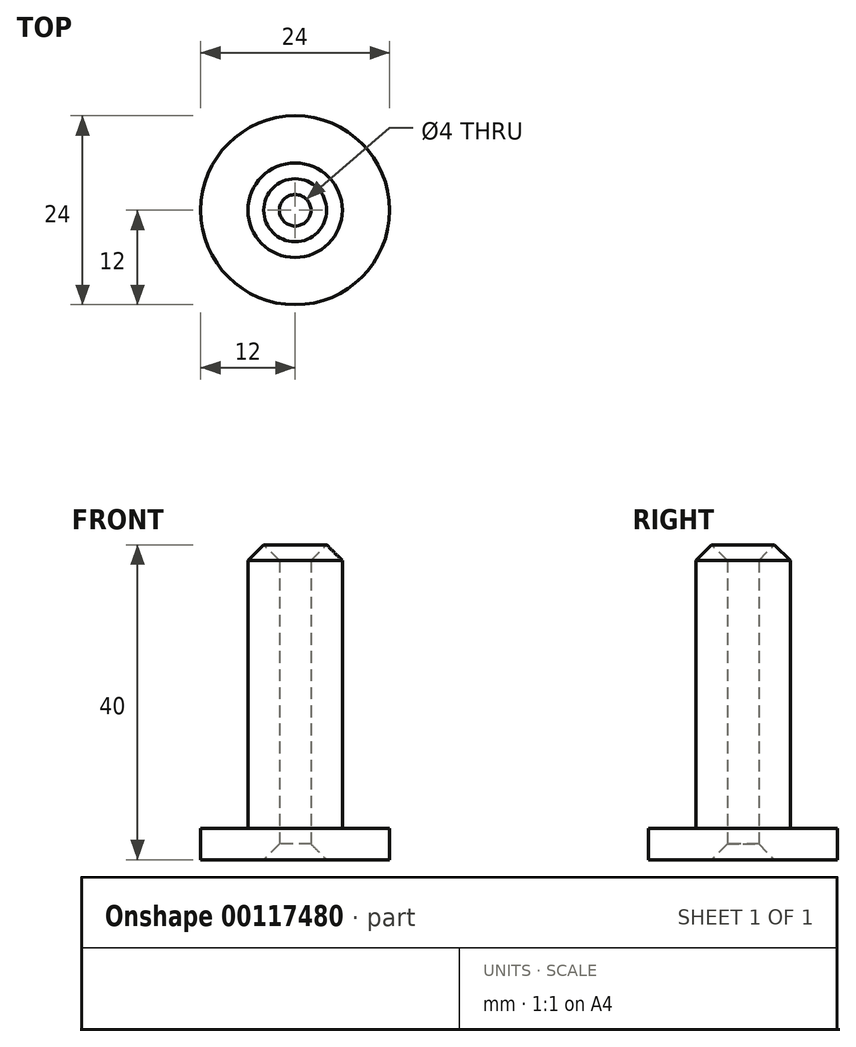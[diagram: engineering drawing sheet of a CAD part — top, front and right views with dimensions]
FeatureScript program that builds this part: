
annotation { "Feature Type Name" : "Feature", "Feature Type Description" : "" }
export const myFeature = defineFeature(function(context is Context, id is Id, definition is map)
    precondition{}
    {
        {
            var Q0;
            Q0=qCreatedBy(makeId("Top.planeOp"),FACE);
            var sketch = newSketch(context, id + "F0", { "sketchPlane" : qUnion([Q0])});
            skCircle(sketch, "E0", {"center": v(0, 0) * mm, "radius": 2 * mm});
            skCircle(sketch, "E1", {"center": v(0, 0) * mm, "radius": 6 * mm});
            skCircle(sketch, "E2", {"center": v(0, 0) * mm, "radius": 12 * mm});
            skSolve(sketch);
        }
        {
            var Q0;
            Q0=makeQuery(id+"F0.imprint","IMPRINT",FACE,{"disambiguationData":[TD([[makeQuery(id+"F0.imprint","IMPRINT",EDGE,{"derivedFrom":sQuery(id+"F0.wireOp",EDGE,"E0")}),-1.0]])]});
            extrude(context, id + "F1", {"entities" : qUnion([Q0]), "depth" : 40 * mm});
        }
        {
            var Q0;
            Q0=makeQuery(id+"F0.imprint","IMPRINT",FACE,{"disambiguationData":[TD([[makeQuery(id+"F0.imprint","IMPRINT",EDGE,{"derivedFrom":sQuery(id+"F0.wireOp",EDGE,"E1")}),-1.0]])]});
            extrude(context, id + "F2", {"entities" : qUnion([Q0]), "operationType" : NewBodyOperationType.ADD, "depth" : 4 * mm});
        }
        {
            var Q0;
            Q0=makeQuery(id+"F1.opExtrude","CAP_EDGE",EDGE,{"disambiguationData":[OSD([sQuery(id+"F0.wireOp",EDGE,"E1")])],"isStart":false});
            var Q1;
            Q1=makeQuery(id+"F1.opExtrude","CAP_EDGE",EDGE,{"disambiguationData":[OSD([sQuery(id+"F0.wireOp",EDGE,"E0")])],"isStart":false});
            var Q2;
            Q2=makeQuery(id+"F1.opExtrude","CAP_EDGE",EDGE,{"disambiguationData":[OSD([sQuery(id+"F0.wireOp",EDGE,"E0")])],"isStart":true});
            chamfer(context, id + "F3", {"entities" : qUnion([Q0, Q1, Q2]), "width" : 2 * mm, "tangentPropagation" : true});
        }
    });
